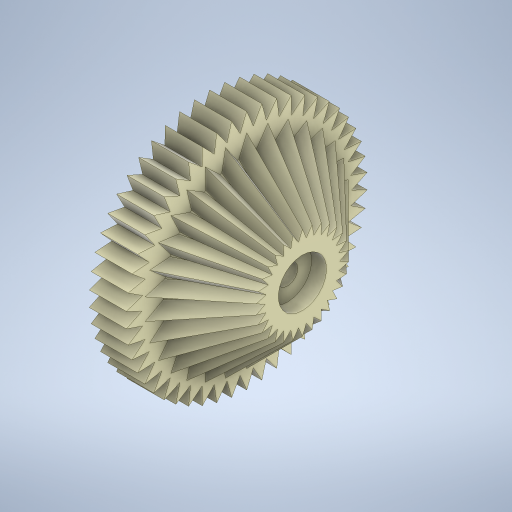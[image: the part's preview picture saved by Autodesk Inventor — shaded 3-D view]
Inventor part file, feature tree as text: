
AUTODESK INVENTOR PART (.ipt)
format: ipt  version: 2023 (Build 270158030, 158C)  size: 588,288 bytes
history: native  units: in
note: dims shown in document units (in); Inventor stores cm internally (conversion verified against a paired STEP export)
features: sketch x7, extrude x4, pattern_circular x2, other x1, loft x1
ambient origin geometry x8: Origin, YZ Plane, XZ Plane, XY Plane, X Axis, Y Axis, Z Axis, Center Point
bodies: Solid1 (feature_tree)
feature tree (15):
  other  "Main Body"
  loft  "Loft3"
  pattern_circular  "Circular Pattern4"  Count=2  [1 undecoded]
  extrude  "Extrusion7"  Depth=1.9685in
  extrude  "Extrusion8"  Depth=0.3937in
  extrude  "Extrusion9"  Depth=0.3937in
  extrude  "Extrusion10"  TaperAngle=0.0deg  [1 undecoded]
  pattern_circular  "Circular Pattern5"  Count=30 Angle=360.0deg
  sketch  "Sketch1"  dims[d1=45.0deg d2=1.1811in]
  sketch  "Sketch16"  dims[d4=90.0deg d50=0.7874in]
  sketch  "Sketch17"  dims[d51=0.3937in d52=1.9685in]
  sketch  "Sketch18"  dims[d53=45.0deg d54=0.3937in]
  sketch  "Sketch19"  dims[d55=45.0deg d56=0.3937in]
  sketch  "Sketch20"  dims[d57=0.0in d58=90.0deg d59=0.0in d60=90.0deg d61=11.811in d62=360.0deg]
  sketch  "Sketch21"  dims[d64=1.0236in d65=0.315in d66=0.0in d67=0.4331in d68=0.0in d69=0.0in d70=1.0236in d71=0.315in d72=0.0in d73=0.3937in d74=45.0deg d75=0.315in d76=0.0in d77=19.685in d78=360.0deg d39=0.0197in d40=0.0344in d41=0.0197in d42=0.0344in]
note: 2 required parameter values undecoded (feature->parameter linkage not recoverable at this tier; creation-order binding heuristic only, values carry confidence <= 0.55)
